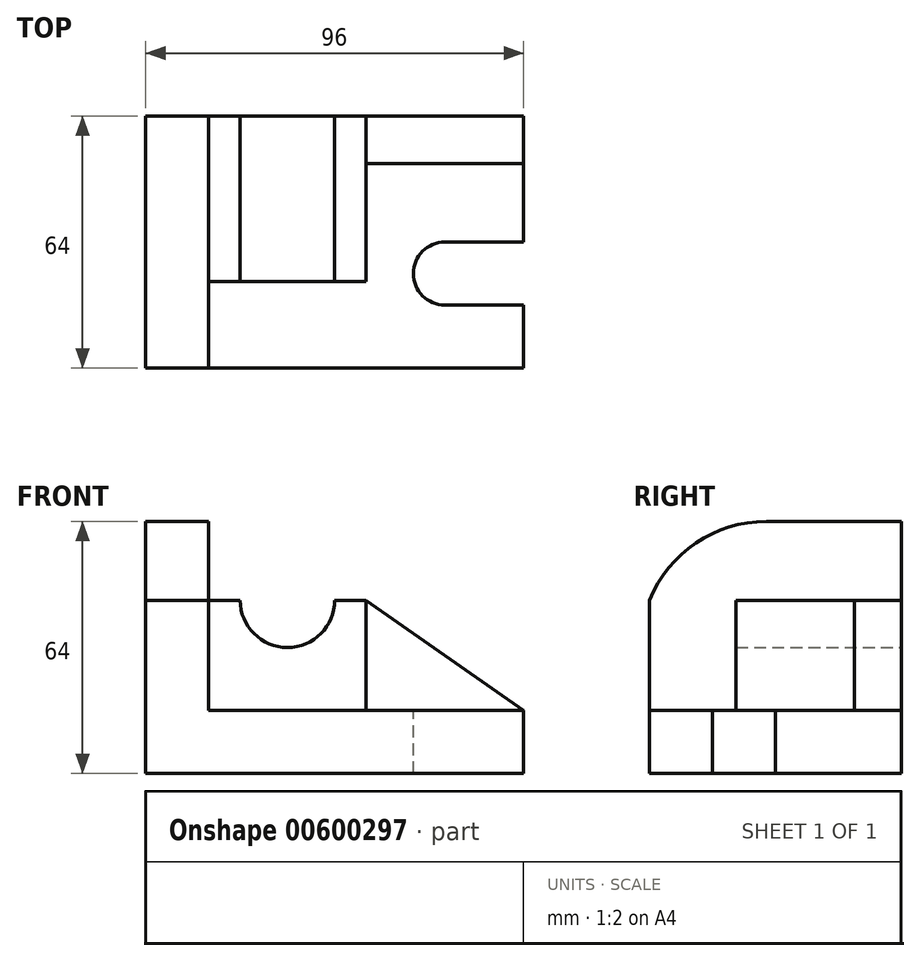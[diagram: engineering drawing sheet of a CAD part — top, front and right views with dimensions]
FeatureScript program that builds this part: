
annotation { "Feature Type Name" : "Feature", "Feature Type Description" : "" }
export const myFeature = defineFeature(function(context is Context, id is Id, definition is map)
    precondition{}
    {
        {
            var Q0;
            Q0=qCreatedBy(makeId("Top.planeOp"),FACE);
            var sketch = newSketch(context, id + "F0", { "sketchPlane" : qUnion([Q0])});
            skLineSegment(sketch, "E0.bottom", {"start": v(-54.25, -6.46) * mm, "end": v(41.75, -6.46) * mm});
            skLineSegment(sketch, "E0.top", {"start": v(-54.25, 57.54) * mm, "end": v(41.75, 57.54) * mm});
            skLineSegment(sketch, "E0.left", {"start": v(-54.25, -6.46) * mm, "end": v(-54.25, 57.54) * mm});
            skLineSegment(sketch, "E0.right", {"start": v(41.75, -6.46) * mm, "end": v(41.75, 57.54) * mm});
            skSolve(sketch);
        }
        {
            var Q0;
            Q0 = qSketchRegion(id + "F0", true);
            extrude(context, id + "F1", {"entities" : qUnion([Q0]), "depth" : 16 * mm, "offsetDistance" : 25 * mm});
        }
        {
            var Q0;
            Q0=makeQuery(id+"F1.opExtrude","SWEPT_FACE",FACE,{"disambiguationData":[OSD([sQuery(id+"F0.wireOp",EDGE,"E0.left")])]});
            var sketch = newSketch(context, id + "F2", { "sketchPlane" : qUnion([Q0])});
            skLineSegment(sketch, "E1", {"start": v(6.46, 16) * mm, "end": v(6.46, 44) * mm});
            skLineSegment(sketch, "E2", {"start": v(-57.54, 16) * mm, "end": v(-57.54, 64) * mm});
            skPoint(sketch, "E2.endSnap0", {"position": v(-57.54, 8) * mm});
            skLineSegment(sketch, "E3", {"start": v(-57.54, 64) * mm, "end": v(-23.2, 64) * mm});
            skArc(sketch, "E4", {"start": v(-23.2, 64) * mm, "mid": v(-5.32, 58.53) * mm, "end": v(6.46, 44) * mm});
            skSolve(sketch);
        }
        {
            var Q0;
            Q0=makeQuery(id+"F2.imprint","IMPRINT",FACE,{"disambiguationData":[TD([[makeQuery(id+"F2.imprint","IMPRINT",EDGE,{"derivedFrom":sQuery(id+"F2.wireOp",EDGE,"E1")}),1.0]])]});
            extrude(context, id + "F3", {"entities" : qUnion([Q0]), "operationType" : NewBodyOperationType.ADD, "oppositeDirection" : true, "depth" : 16 * mm, "offsetDistance" : 25 * mm});
        }
        {
            var Q0;
            Q0=makeQuery(id+"F1.opExtrude","CAP_FACE",FACE,{"disambiguationData":[OSD([sQuery(id+"F0.wireOp",EDGE,"E0.bottom"),sQuery(id+"F0.wireOp",EDGE,"E0.top"),sQuery(id+"F0.wireOp",EDGE,"E0.left"),sQuery(id+"F0.wireOp",EDGE,"E0.right")])],"isStart":false});
            var sketch = newSketch(context, id + "F4", { "sketchPlane" : qUnion([Q0])});
            skLineSegment(sketch, "E5", {"start": v(41.75, 9.54) * mm, "end": v(21.75, 9.54) * mm});
            skLineSegment(sketch, "E6", {"start": v(41.75, 25.54) * mm, "end": v(21.75, 25.54) * mm});
            skArc(sketch, "E7", {"start": v(21.75, 9.54) * mm, "mid": v(13.75, 17.54) * mm, "end": v(21.75, 25.54) * mm});
            skLineSegment(sketch, "E8", {"start": v(41.75, 9.54) * mm, "end": v(41.75, 25.54) * mm});
            skSolve(sketch);
        }
        {
            var Q0;
            Q0=makeQuery(id+"F4.imprint","IMPRINT",FACE,{"disambiguationData":[TD([[makeQuery(id+"F4.imprint","IMPRINT",EDGE,{"derivedFrom":sQuery(id+"F4.wireOp",EDGE,"E5")}),-1.0]])]});
            extrude(context, id + "F5", {"entities" : qUnion([Q0]), "operationType" : NewBodyOperationType.REMOVE, "oppositeDirection" : true, "depth" : 16 * mm, "offsetDistance" : 25 * mm});
        }
        {
            var Q0;
            Q0=makeQuery(id+"F3.boolean.opBoolean","MERGE",FACE,{"derivedFrom":[makeQuery(id+"F1.opExtrude","SWEPT_FACE",FACE,{"disambiguationData":[OSD([sQuery(id+"F0.wireOp",EDGE,"E0.top")])]}),makeQuery(id+"F3.opExtrude","SWEPT_FACE",FACE,{"disambiguationData":[OSD([sQuery(id+"F2.wireOp",EDGE,"E2")])]})]});
            var sketch = newSketch(context, id + "F6", { "sketchPlane" : qUnion([Q0])});
            skLineSegment(sketch, "E9.bottom", {"start": v(38.25, 16) * mm, "end": v(-1.75, 16) * mm});
            skLineSegment(sketch, "E9.top", {"start": v(38.25, 44) * mm, "end": v(-1.75, 44) * mm});
            skLineSegment(sketch, "E9.left", {"start": v(38.25, 16) * mm, "end": v(38.25, 44) * mm});
            skLineSegment(sketch, "E9.right", {"start": v(-1.75, 16) * mm, "end": v(-1.75, 44) * mm});
            skSolve(sketch);
        }
        {
            var Q0;
            Q0 = qSketchRegion(id + "F6", true);
            extrude(context, id + "F7", {"entities" : qUnion([Q0]), "operationType" : NewBodyOperationType.ADD, "oppositeDirection" : true, "depth" : 42 * mm, "offsetDistance" : 25 * mm});
        }
        {
            var Q0;
            Q0=makeQuery(id+"F7.boolean.opBoolean","MERGE",FACE,{"derivedFrom":[makeQuery(id+"F3.boolean.opBoolean","MERGE",FACE,{"derivedFrom":[makeQuery(id+"F1.opExtrude","SWEPT_FACE",FACE,{"disambiguationData":[OSD([sQuery(id+"F0.wireOp",EDGE,"E0.top")])]}),makeQuery(id+"F3.opExtrude","SWEPT_FACE",FACE,{"disambiguationData":[OSD([sQuery(id+"F2.wireOp",EDGE,"E2")])]})]}),makeQuery(id+"F7.opExtrude","CAP_FACE",FACE,{"disambiguationData":[OSD([sQuery(id+"F6.wireOp",EDGE,"E9.bottom"),sQuery(id+"F6.wireOp",EDGE,"E9.top"),sQuery(id+"F6.wireOp",EDGE,"E9.left"),sQuery(id+"F6.wireOp",EDGE,"E9.right")])],"isStart":true})]});
            var sketch = newSketch(context, id + "F8", { "sketchPlane" : qUnion([Q0])});
            skArc(sketch, "E10", {"start": v(30.25, 44) * mm, "mid": v(18.25, 32) * mm, "end": v(6.25, 44) * mm});
            skLineSegment(sketch, "E11", {"start": v(6.25, 44) * mm, "end": v(30.25, 44) * mm});
            skSolve(sketch);
        }
        {
            var Q0;
            Q0 = qSketchRegion(id + "F8", true);
            extrude(context, id + "F9", {"entities" : qUnion([Q0]), "operationType" : NewBodyOperationType.REMOVE, "oppositeDirection" : true, "depth" : 42 * mm, "offsetDistance" : 25 * mm});
        }
        {
            var Q0;
            Q0=makeQuery(id+"F7.boolean.opBoolean","MERGE",FACE,{"derivedFrom":[makeQuery(id+"F3.boolean.opBoolean","MERGE",FACE,{"derivedFrom":[makeQuery(id+"F1.opExtrude","SWEPT_FACE",FACE,{"disambiguationData":[OSD([sQuery(id+"F0.wireOp",EDGE,"E0.top")])]}),makeQuery(id+"F3.opExtrude","SWEPT_FACE",FACE,{"disambiguationData":[OSD([sQuery(id+"F2.wireOp",EDGE,"E2")])]})]}),makeQuery(id+"F7.opExtrude","CAP_FACE",FACE,{"disambiguationData":[OSD([sQuery(id+"F6.wireOp",EDGE,"E9.bottom"),sQuery(id+"F6.wireOp",EDGE,"E9.top"),sQuery(id+"F6.wireOp",EDGE,"E9.left"),sQuery(id+"F6.wireOp",EDGE,"E9.right")])],"isStart":true})]});
            var sketch = newSketch(context, id + "F10", { "sketchPlane" : qUnion([Q0])});
            skLineSegment(sketch, "E12", {"start": v(-1.75, 16) * mm, "end": v(-41.75, 16) * mm});
            skLineSegment(sketch, "E13", {"start": v(-41.75, 16) * mm, "end": v(-1.75, 44) * mm});
            skLineSegment(sketch, "E14", {"start": v(-1.75, 44) * mm, "end": v(-1.75, 16) * mm});
            skSolve(sketch);
        }
        {
            var Q0;
            Q0 = qSketchRegion(id + "F10", true);
            extrude(context, id + "F11", {"entities" : qUnion([Q0]), "operationType" : NewBodyOperationType.ADD, "oppositeDirection" : true, "depth" : 12 * mm, "offsetDistance" : 25 * mm});
        }
    });
